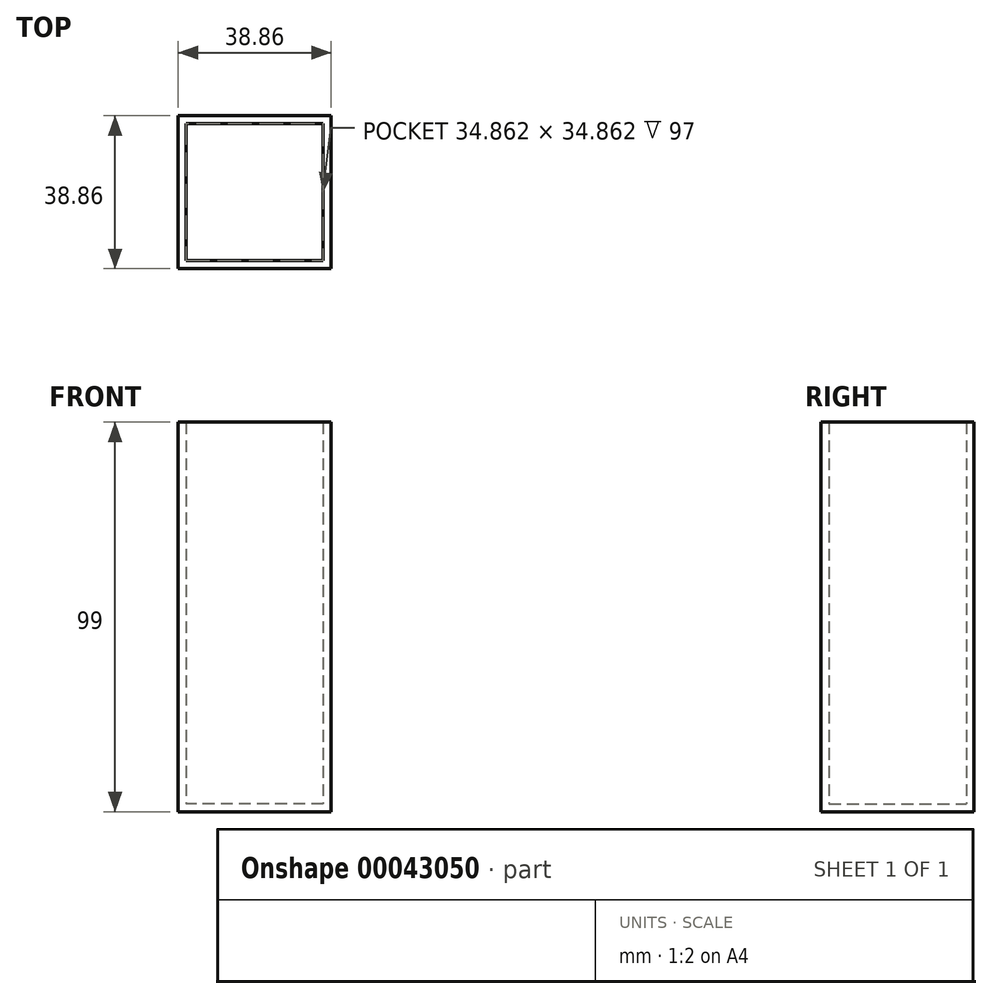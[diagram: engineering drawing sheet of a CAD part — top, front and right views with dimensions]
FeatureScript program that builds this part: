
annotation { "Feature Type Name" : "Feature", "Feature Type Description" : "" }
export const myFeature = defineFeature(function(context is Context, id is Id, definition is map)
    precondition{}
    {
        {
            var Q0;
            Q0=qCreatedBy(makeId("Top.planeOp"),FACE);
            var sketch = newSketch(context, id + "F0", { "sketchPlane" : qUnion([Q0])});
            skLineSegment(sketch, "E0.rect.bottom", {"start": v(19.43, -19.43) * mm, "end": v(-19.43, -19.43) * mm});
            skLineSegment(sketch, "E0.rect.top", {"start": v(19.43, 19.43) * mm, "end": v(-19.43, 19.43) * mm});
            skLineSegment(sketch, "E0.rect.left", {"start": v(19.43, -19.43) * mm, "end": v(19.43, 19.43) * mm});
            skLineSegment(sketch, "E0.rect.right", {"start": v(-19.43, -19.43) * mm, "end": v(-19.43, 19.43) * mm});
            skPoint(sketch, "E0.rect.middle", {"position": v(0, 0) * mm});
            skLineSegment(sketch, "E1.0", {"start": v(17.43, -17.43) * mm, "end": v(17.43, 17.43) * mm});
            skLineSegment(sketch, "E1.1", {"start": v(17.43, -17.43) * mm, "end": v(-17.43, -17.43) * mm});
            skLineSegment(sketch, "E1.2", {"start": v(-17.43, -17.43) * mm, "end": v(-17.43, 17.43) * mm});
            skLineSegment(sketch, "E1.3", {"start": v(17.43, 17.43) * mm, "end": v(-17.43, 17.43) * mm});
            skSolve(sketch);
        }
        {
            var Q0;
            Q0=makeQuery(id+"F0.imprint","IMPRINT",FACE,{"disambiguationData":[TD([[makeQuery(id+"F0.imprint","IMPRINT",EDGE,{"derivedFrom":sQuery(id+"F0.wireOp",EDGE,"E0.rect.bottom")}),-1.0]])]});
            extrude(context, id + "F1", {"entities" : qUnion([Q0]), "depth" : 97 * mm});
        }
        {
            var Q0;
            Q0=makeQuery(id+"F0.imprint","IMPRINT",FACE,{"disambiguationData":[TD([[makeQuery(id+"F0.imprint","IMPRINT",EDGE,{"derivedFrom":sQuery(id+"F0.wireOp",EDGE,"E1.0")}),1.0]])]});
            var Q1;
            Q1=makeQuery(id+"F0.imprint","IMPRINT",FACE,{"disambiguationData":[TD([[makeQuery(id+"F0.imprint","IMPRINT",EDGE,{"derivedFrom":sQuery(id+"F0.wireOp",EDGE,"E0.rect.bottom")}),-1.0]])]});
            extrude(context, id + "F2", {"entities" : qUnion([Q0, Q1]), "operationType" : NewBodyOperationType.ADD, "oppositeDirection" : true, "depth" : 2 * mm});
        }
    });
